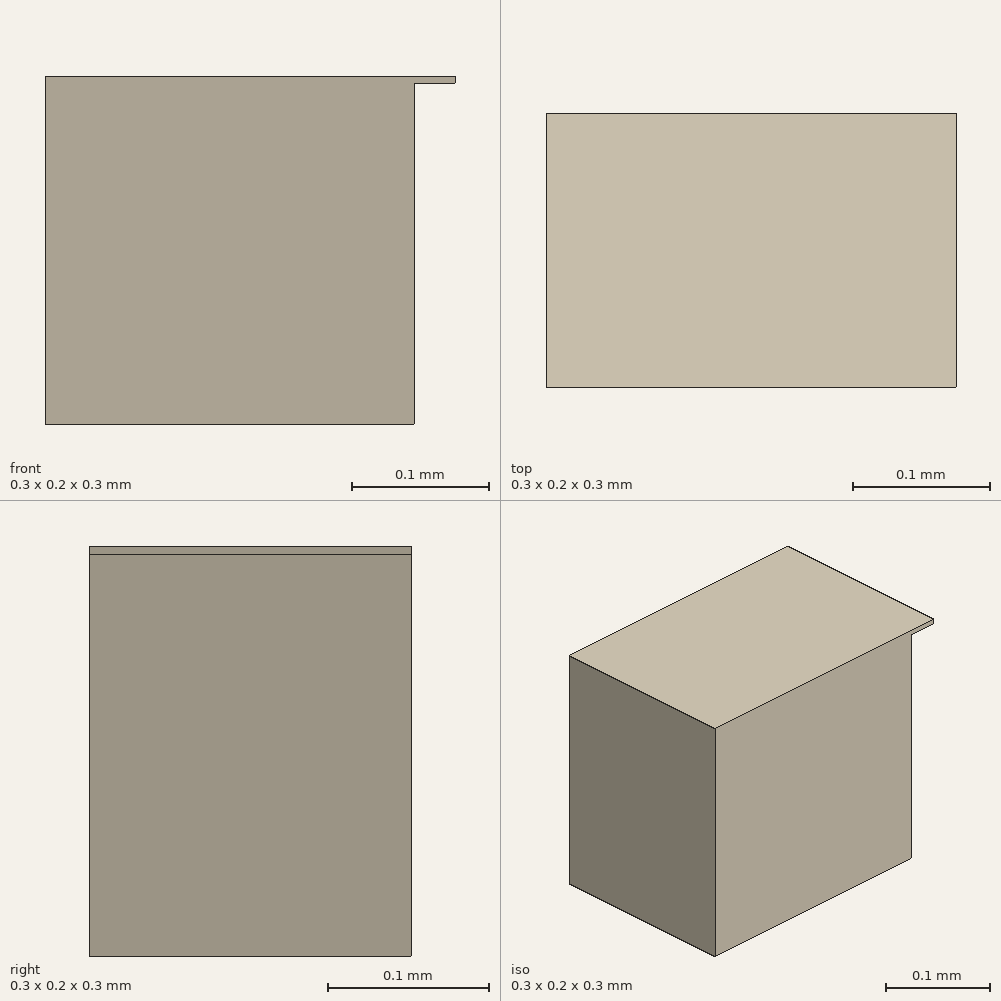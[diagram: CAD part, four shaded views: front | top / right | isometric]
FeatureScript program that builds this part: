
annotation { "Feature Type Name" : "Feature", "Feature Type Description" : "" }
export const myFeature = defineFeature(function(context is Context, id is Id, definition is map)
    precondition{}
    {
        {
            var Q0;
            Q0=qCreatedBy(makeId("Top.planeOp"),FACE);
            var sketch = newSketch(context, id + "F0", { "sketchPlane" : qUnion([Q0])});
            skLineSegment(sketch, "E0.bottom", {"start": v(-0.1, 0.1) * mm, "end": v(0.17, 0.1) * mm});
            skLineSegment(sketch, "E0.top", {"start": v(-0.1, -0.1) * mm, "end": v(0.17, -0.1) * mm});
            skLineSegment(sketch, "E0.left", {"start": v(-0.1, 0.1) * mm, "end": v(-0.1, -0.1) * mm});
            skLineSegment(sketch, "E0.right", {"start": v(0.17, 0.1) * mm, "end": v(0.17, -0.1) * mm});
            skSolve(sketch);
        }
        {
            var Q0;
            Q0 = qSketchRegion(id + "F0", true);
            extrude(context, id + "F1", {"entities" : qUnion([Q0]), "depth" : 0.25 * mm, "offsetDistance" : 25 * mm});
        }
        {
            var Q0;
            Q0=qCreatedBy(makeId("Top.planeOp"),FACE);
            cPlane(context, id + "F2", {"entities" : qUnion([Q0]), "cplaneType" : CPlaneType.OFFSET, "offset" : 0.25 * mm, "width" : 150 * mm, "height" : 150 * mm});
        }
        {
            var Q0;
            Q0=qCreatedBy(id+"F2.planeOp",FACE);
            var sketch = newSketch(context, id + "F3", { "sketchPlane" : qUnion([Q0])});
            skLineSegment(sketch, "E1.bottom", {"start": v(0.2, 0.1) * mm, "end": v(-0.1, 0.1) * mm});
            skLineSegment(sketch, "E1.top", {"start": v(0.2, -0.1) * mm, "end": v(-0.1, -0.1) * mm});
            skLineSegment(sketch, "E1.left", {"start": v(0.2, 0.1) * mm, "end": v(0.2, -0.1) * mm});
            skLineSegment(sketch, "E1.right", {"start": v(-0.1, 0.1) * mm, "end": v(-0.1, -0.1) * mm});
            skSolve(sketch);
        }
        {
            var Q0;
            Q0 = qSketchRegion(id + "F3", true);
            extrude(context, id + "F4", {"entities" : qUnion([Q0]), "operationType" : NewBodyOperationType.ADD, "depth" : 0 * mm, "offsetDistance" : 25 * mm});
        }
    });
